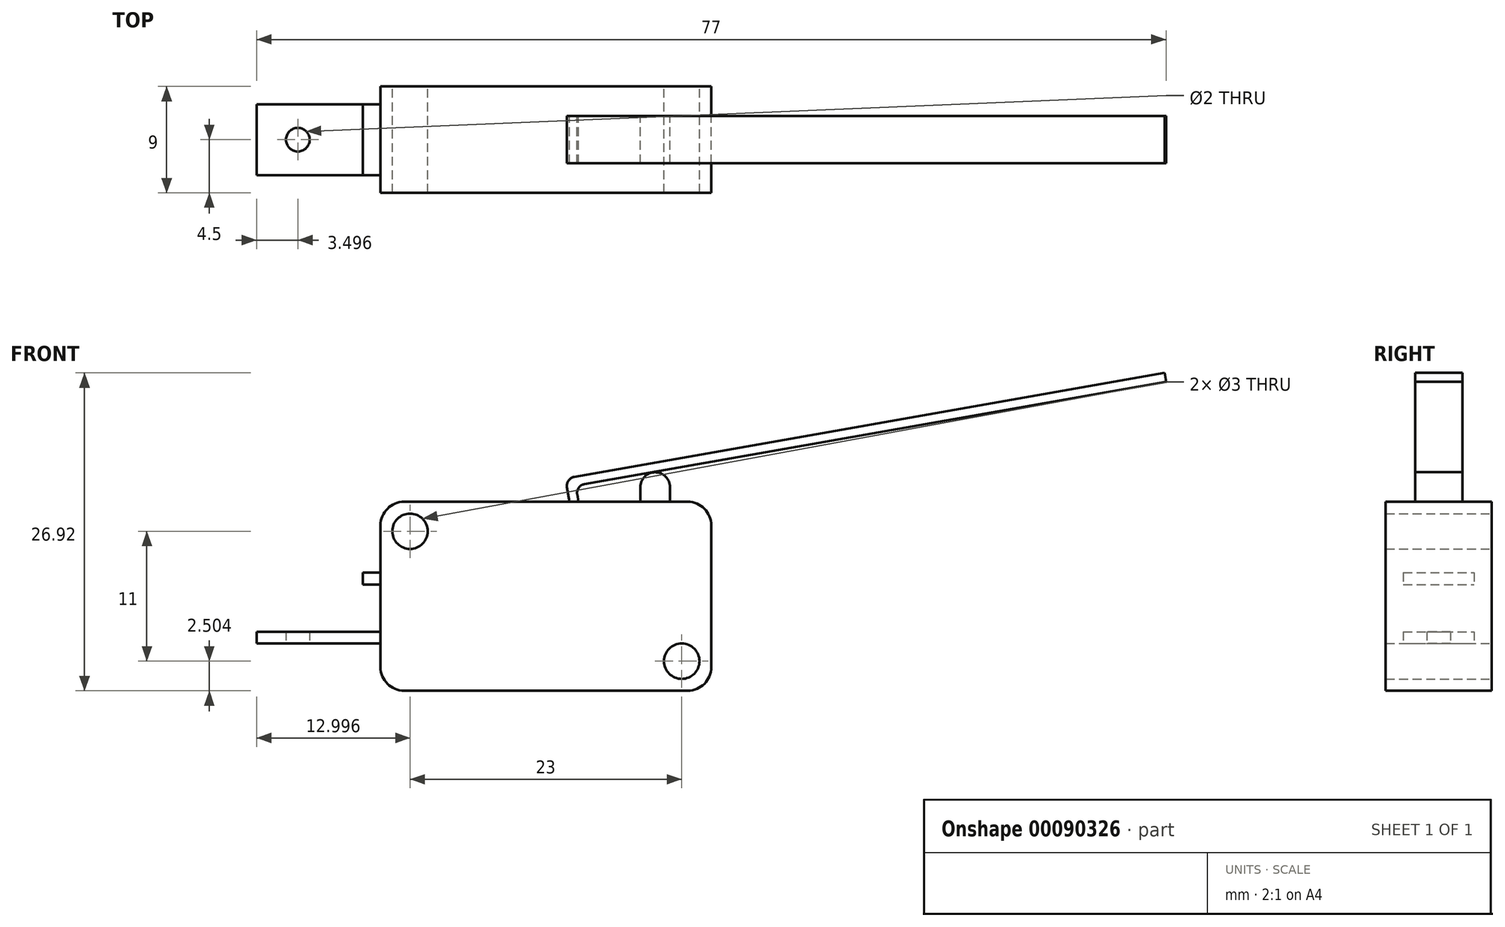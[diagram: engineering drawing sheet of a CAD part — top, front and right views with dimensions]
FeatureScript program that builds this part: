
annotation { "Feature Type Name" : "Feature", "Feature Type Description" : "" }
export const myFeature = defineFeature(function(context is Context, id is Id, definition is map)
    precondition{}
    {
        {
            var Q0;
            Q0=qCreatedBy(makeId("Front.planeOp"),FACE);
            var sketch = newSketch(context, id + "F0", { "sketchPlane" : qUnion([Q0])});
            skLineSegment(sketch, "E0.bottom", {"start": v(2.12, 15.36) * mm, "end": v(26.12, 15.36) * mm});
            skLineSegment(sketch, "E0.top", {"start": v(2.12, -0.64) * mm, "end": v(26.12, -0.64) * mm});
            skLineSegment(sketch, "E0.left", {"start": v(0.12, 13.36) * mm, "end": v(0.12, 1.36) * mm});
            skLineSegment(sketch, "E0.right", {"start": v(28.12, 13.36) * mm, "end": v(28.12, 1.36) * mm});
            skPoint(sketch, "E1.visualSharp", {"position": v(0.12, 15.36) * mm});
            skArc(sketch, "E1.filletArc", {"start": v(2.12, 15.36) * mm, "mid": v(0.7, 14.78) * mm, "end": v(0.12, 13.36) * mm});
            skPoint(sketch, "E2.visualSharp", {"position": v(28.12, 15.36) * mm});
            skArc(sketch, "E2.filletArc", {"start": v(28.12, 13.36) * mm, "mid": v(27.53, 14.78) * mm, "end": v(26.12, 15.36) * mm});
            skPoint(sketch, "E3.visualSharp", {"position": v(28.12, -0.64) * mm});
            skArc(sketch, "E3.filletArc", {"start": v(26.12, -0.64) * mm, "mid": v(27.53, -0.05) * mm, "end": v(28.12, 1.36) * mm});
            skPoint(sketch, "E4.visualSharp", {"position": v(0.12, -0.64) * mm});
            skArc(sketch, "E4.filletArc", {"start": v(0.12, 1.36) * mm, "mid": v(0.7, -0.05) * mm, "end": v(2.12, -0.64) * mm});
            skPoint(sketch, "E5", {"position": v(2.62, 15.36) * mm});
            skPoint(sketch, "E6", {"position": v(0.12, 12.86) * mm});
            skPoint(sketch, "E7", {"position": v(2.62, 12.86) * mm});
            skCircle(sketch, "E8", {"center": v(2.62, 12.86) * mm, "radius": 1.5 * mm});
            skPoint(sketch, "E9", {"position": v(25.62, -0.64) * mm});
            skPoint(sketch, "E10", {"position": v(25.62, 1.86) * mm});
            skCircle(sketch, "E11", {"center": v(25.62, 1.86) * mm, "radius": 1.5 * mm});
            skPoint(sketch, "E12", {"position": v(16.12, 15.36) * mm});
            skPoint(sketch, "E13", {"position": v(0.12, 9.36) * mm});
            skLineSegment(sketch, "E14.bottom", {"start": v(0.12, 9.36) * mm, "end": v(-1.38, 9.36) * mm});
            skLineSegment(sketch, "E14.top", {"start": v(0.12, 8.36) * mm, "end": v(-1.38, 8.36) * mm});
            skLineSegment(sketch, "E14.left", {"start": v(0.12, 9.36) * mm, "end": v(0.12, 8.36) * mm});
            skLineSegment(sketch, "E14.right", {"start": v(-1.38, 9.36) * mm, "end": v(-1.38, 8.36) * mm});
            skLineSegment(sketch, "E15", {"start": v(16.12, 15.36) * mm, "end": v(15.9, 16.6) * mm});
            skLineSegment(sketch, "E16", {"start": v(16.88, 15.36) * mm, "end": v(16.77, 15.99) * mm});
            skLineSegment(sketch, "E17", {"start": v(16.5, 17.46) * mm, "end": v(16.5, 17.46) * mm});
            skLineSegment(sketch, "E18", {"start": v(15.77, 17.33) * mm, "end": v(66.49, 26.28) * mm});
            skLineSegment(sketch, "E19", {"start": v(66.49, 26.28) * mm, "end": v(66.62, 25.54) * mm});
            skLineSegment(sketch, "E20", {"start": v(66.62, 25.54) * mm, "end": v(17.38, 16.86) * mm});
            skPoint(sketch, "E21.visualSharp", {"position": v(15.77, 17.33) * mm});
            skArc(sketch, "E21.filletArc", {"start": v(16.5, 17.46) * mm, "mid": v(16.02, 17.16) * mm, "end": v(15.9, 16.6) * mm});
            skPoint(sketch, "E22.newPointB", {"position": v(16.5, 17.46) * mm});
            skArc(sketch, "E22.filletArc", {"start": v(17.38, 16.86) * mm, "mid": v(16.9, 16.55) * mm, "end": v(16.77, 15.99) * mm});
            skPoint(sketch, "E23", {"position": v(24.62, 15.36) * mm});
            skLineSegment(sketch, "E24.bottom", {"start": v(24.62, 15.36) * mm, "end": v(22.12, 15.36) * mm});
            skLineSegment(sketch, "E24.top", {"start": v(24.62, 16.61) * mm, "end": v(22.12, 16.61) * mm});
            skLineSegment(sketch, "E24.left", {"start": v(24.62, 15.36) * mm, "end": v(24.62, 16.61) * mm});
            skLineSegment(sketch, "E24.right", {"start": v(22.12, 15.36) * mm, "end": v(22.12, 16.61) * mm});
            skCircle(sketch, "E25", {"center": v(23.37, 16.61) * mm, "radius": 1.25 * mm});
            skPoint(sketch, "E26", {"position": v(0.12, 3.36) * mm});
            skLineSegment(sketch, "E27.bottom", {"start": v(0.12, 3.36) * mm, "end": v(-10.38, 3.36) * mm});
            skLineSegment(sketch, "E27.top", {"start": v(0.12, 4.36) * mm, "end": v(-10.38, 4.36) * mm});
            skLineSegment(sketch, "E27.left", {"start": v(0.12, 3.36) * mm, "end": v(0.12, 4.36) * mm});
            skLineSegment(sketch, "E27.right", {"start": v(-10.38, 3.36) * mm, "end": v(-10.38, 4.36) * mm});
            skPoint(sketch, "E28", {"position": v(11.62, -0.64) * mm});
            skLineSegment(sketch, "E29.bottom", {"start": v(11.62, -0.64) * mm, "end": v(12.37, -0.64) * mm});
            skLineSegment(sketch, "E29.left", {"start": v(11.62, -0.64) * mm, "end": v(11.62, -3.87) * mm});
            skLineSegment(sketch, "E29.right", {"start": v(12.37, -0.64) * mm, "end": v(12.37, -3.37) * mm});
            skLineSegment(sketch, "E30.bottom", {"start": v(10.87, -4.87) * mm, "end": v(2.87, -4.87) * mm});
            skLineSegment(sketch, "E30.top", {"start": v(11.12, -4.37) * mm, "end": v(2.87, -4.37) * mm});
            skLineSegment(sketch, "E30.right", {"start": v(2.87, -4.87) * mm, "end": v(2.87, -4.37) * mm});
            skPoint(sketch, "E31.visualSharp", {"position": v(12.37, -4.87) * mm});
            skArc(sketch, "E31.filletArc", {"start": v(10.87, -4.87) * mm, "mid": v(11.93, -4.43) * mm, "end": v(12.37, -3.37) * mm});
            skPoint(sketch, "E32.newPointB", {"position": v(13.76, -4.37) * mm});
            skArc(sketch, "E32.filletArc", {"start": v(11.12, -4.37) * mm, "mid": v(11.47, -4.22) * mm, "end": v(11.62, -3.87) * mm});
            skLineSegment(sketch, "E33", {"start": v(66.49, 26.28) * mm, "end": v(-10.38, 26.28) * mm});
            skLineSegment(sketch, "E34", {"start": v(-10.38, 26.28) * mm, "end": v(-10.38, 4.36) * mm});
            skSolve(sketch);
        }
        {
            var Q0;
            Q0=makeQuery(id+"F0.imprint","IMPRINT",FACE,{"disambiguationData":[TD([[makeQuery(id+"F0.imprint","IMPRINT",EDGE,{"derivedFrom":sQuery(id+"F0.wireOp",EDGE,"E0.right")}),-1.0]])]});
            extrude(context, id + "F1", {"entities" : qUnion([Q0]), "depth" : 4.5 * mm});
        }
        {
            var Q0;
            Q0=makeQuery(id+"F0.imprint","IMPRINT",FACE,{"disambiguationData":[TD([[makeQuery(id+"F0.imprint","IMPRINT",EDGE,{"derivedFrom":sQuery(id+"F0.wireOp",EDGE,"E14.bottom")}),1.0]])]});
            var Q1;
            Q1=makeQuery(id+"F0.imprint","IMPRINT",FACE,{"disambiguationData":[TD([[makeQuery(id+"F0.imprint","IMPRINT",EDGE,{"derivedFrom":sQuery(id+"F0.wireOp",EDGE,"E27.bottom")}),-1.0]])]});
            var Q2;
            Q2=makeQuery(id+"F0.imprint","IMPRINT",FACE,{"disambiguationData":[TD([[makeQuery(id+"F0.imprint","IMPRINT",EDGE,{"derivedFrom":sQuery(id+"F0.wireOp",EDGE,"E29.bottom")}),-1.0]])]});
            extrude(context, id + "F2", {"entities" : qUnion([Q0, Q1, Q2]), "operationType" : NewBodyOperationType.ADD, "depth" : 3 * mm});
        }
        {
            var Q0;
            {var subQ4=sQuery(id+"F0.wireOp",EDGE,"E15");Q0=makeQuery(id+"F0.imprint","IMPRINT",FACE,{"disambiguationData":[TD([[makeQuery(id+"F0.imprint","IMPRINT",EDGE,{"derivedFrom":subQ4}),-1.0]])]});}
            var Q1;
            {var subQ0=sQuery(id+"F0.wireOp",EDGE,"E24.left");Q1=makeQuery(id+"F0.imprint","IMPRINT",FACE,{"disambiguationData":[TD([[makeQuery(id+"F0.imprint","IMPRINT",EDGE,{"derivedFrom":subQ0}),1.0]])]});}
            var Q2;
            {var subQ0=sQuery(id+"F0.wireOp",EDGE,"E24.right");Q2=makeQuery(id+"F0.imprint","IMPRINT",FACE,{"disambiguationData":[TD([[makeQuery(id+"F0.imprint","IMPRINT",EDGE,{"derivedFrom":subQ0}),-1.0]])]});}
            var Q3;
            {var subQ0=sQuery(id+"F0.wireOp",EDGE,"E24.top");Q3=makeQuery(id+"F0.imprint","IMPRINT",FACE,{"disambiguationData":[TD([[makeQuery(id+"F0.imprint","IMPRINT",EDGE,{"derivedFrom":subQ0}),1.0]])]});}
            var Q4;
            {var subQ0=sQuery(id+"F0.wireOp",EDGE,"E24.top");Q4=makeQuery(id+"F0.imprint","IMPRINT",FACE,{"disambiguationData":[TD([[makeQuery(id+"F0.imprint","IMPRINT",EDGE,{"derivedFrom":subQ0}),-1.0]])]});}
            extrude(context, id + "F3", {"entities" : qUnion([Q0, Q1, Q2, Q3, Q4]), "operationType" : NewBodyOperationType.ADD, "depth" : 2 * mm});
        }
        {
            var Q0;
            Q0=makeQuery(id+"F0.imprint","IMPRINT",FACE,{"disambiguationData":[TD([[makeQuery(id+"F0.imprint","IMPRINT",EDGE,{"derivedFrom":sQuery(id+"F0.wireOp",EDGE,"E0.right")}),-1.0]])]});
            extrude(context, id + "F4", {"entities" : qUnion([Q0]), "operationType" : NewBodyOperationType.ADD, "oppositeDirection" : true, "depth" : 4.5 * mm});
        }
        {
            var Q0;
            Q0=makeQuery(id+"F0.imprint","IMPRINT",FACE,{"disambiguationData":[TD([[makeQuery(id+"F0.imprint","IMPRINT",EDGE,{"derivedFrom":sQuery(id+"F0.wireOp",EDGE,"E14.bottom")}),1.0]])]});
            var Q1;
            Q1=makeQuery(id+"F0.imprint","IMPRINT",FACE,{"disambiguationData":[TD([[makeQuery(id+"F0.imprint","IMPRINT",EDGE,{"derivedFrom":sQuery(id+"F0.wireOp",EDGE,"E27.bottom")}),-1.0]])]});
            var Q2;
            Q2=makeQuery(id+"F0.imprint","IMPRINT",FACE,{"disambiguationData":[TD([[makeQuery(id+"F0.imprint","IMPRINT",EDGE,{"derivedFrom":sQuery(id+"F0.wireOp",EDGE,"E29.bottom")}),-1.0]])]});
            extrude(context, id + "F5", {"entities" : qUnion([Q0, Q1, Q2]), "operationType" : NewBodyOperationType.ADD, "oppositeDirection" : true, "depth" : 3 * mm});
        }
        {
            var Q0;
            {var subQ0=sQuery(id+"F0.wireOp",EDGE,"E24.top");Q0=makeQuery(id+"F0.imprint","IMPRINT",FACE,{"disambiguationData":[TD([[makeQuery(id+"F0.imprint","IMPRINT",EDGE,{"derivedFrom":subQ0}),-1.0]])]});}
            var Q1;
            {var subQ0=sQuery(id+"F0.wireOp",EDGE,"E24.top");Q1=makeQuery(id+"F0.imprint","IMPRINT",FACE,{"disambiguationData":[TD([[makeQuery(id+"F0.imprint","IMPRINT",EDGE,{"derivedFrom":subQ0}),1.0]])]});}
            var Q2;
            {var subQ0=sQuery(id+"F0.wireOp",EDGE,"E24.left");Q2=makeQuery(id+"F0.imprint","IMPRINT",FACE,{"disambiguationData":[TD([[makeQuery(id+"F0.imprint","IMPRINT",EDGE,{"derivedFrom":subQ0}),1.0]])]});}
            var Q3;
            {var subQ0=sQuery(id+"F0.wireOp",EDGE,"E24.right");Q3=makeQuery(id+"F0.imprint","IMPRINT",FACE,{"disambiguationData":[TD([[makeQuery(id+"F0.imprint","IMPRINT",EDGE,{"derivedFrom":subQ0}),-1.0]])]});}
            var Q4;
            {var subQ4=sQuery(id+"F0.wireOp",EDGE,"E15");Q4=makeQuery(id+"F0.imprint","IMPRINT",FACE,{"disambiguationData":[TD([[makeQuery(id+"F0.imprint","IMPRINT",EDGE,{"derivedFrom":subQ4}),-1.0]])]});}
            extrude(context, id + "F6", {"entities" : qUnion([Q0, Q1, Q2, Q3, Q4]), "operationType" : NewBodyOperationType.ADD, "oppositeDirection" : true, "depth" : 2 * mm});
        }
        {
            var Q0;
            {var subQ0=sQuery(id+"F0.wireOp",EDGE,"E30.bottom");Q0=makeQuery(id+"F5.boolean.opBoolean","MERGE",FACE,{"derivedFrom":[makeQuery(id+"F2.opExtrude","SWEPT_FACE",FACE,{"disambiguationData":[OSD([subQ0])]}),makeQuery(id+"F5.opExtrude","SWEPT_FACE",FACE,{"disambiguationData":[OSD([subQ0])]})]});}
            var sketch = newSketch(context, id + "F7", { "sketchPlane" : qUnion([Q0])});
            skPoint(sketch, "E35", {"position": v(2.87, 0) * mm});
            skLineSegment(sketch, "E36", {"start": v(2.87, 0) * mm, "end": v(5.37, 0) * mm});
            skSolve(sketch);
        }
        {
            var Q0;
            {var subQ0=sQuery(id+"F0.wireOp",EDGE,"E27.bottom");Q0=makeQuery(id+"F5.boolean.opBoolean","MERGE",FACE,{"derivedFrom":[makeQuery(id+"F2.opExtrude","SWEPT_FACE",FACE,{"disambiguationData":[OSD([subQ0])]}),makeQuery(id+"F5.opExtrude","SWEPT_FACE",FACE,{"disambiguationData":[OSD([subQ0])]})]});}
            var sketch = newSketch(context, id + "F8", { "sketchPlane" : qUnion([Q0])});
            skPoint(sketch, "E37", {"position": v(-10.38, 0) * mm});
            skLineSegment(sketch, "E38", {"start": v(-10.38, 0) * mm, "end": v(-6.88, 0) * mm});
            skSolve(sketch);
        }
        {
            var Q0;
            Q0=sQuery(id+"F7.wireOp",VERTEX,"E36.end");
            var Q1;
            Q1=sQuery(id+"F8.wireOp",VERTEX,"E38.end");
            var Q2;
            Q2=makeQuery(id+"F1.opExtrude","SWEPT_BODY",BODY,{"disambiguationData":[OSD([sQuery(id+"F0.wireOp",EDGE,"E0.bottom"),sQuery(id+"F0.wireOp",EDGE,"E0.top"),sQuery(id+"F0.wireOp",EDGE,"E0.left"),sQuery(id+"F0.wireOp",EDGE,"E0.right"),sQuery(id+"F0.wireOp",EDGE,"E1.filletArc"),sQuery(id+"F0.wireOp",EDGE,"E2.filletArc"),sQuery(id+"F0.wireOp",EDGE,"E3.filletArc"),sQuery(id+"F0.wireOp",EDGE,"E4.filletArc"),sQuery(id+"F0.wireOp",EDGE,"E8"),sQuery(id+"F0.wireOp",EDGE,"E11"),sQuery(id+"F0.wireOp",EDGE,"E14.left"),sQuery(id+"F0.wireOp",EDGE,"E24.bottom"),sQuery(id+"F0.wireOp",EDGE,"E27.left"),sQuery(id+"F0.wireOp",EDGE,"E29.bottom")])]});
            hole(context, id + "F9", {"style" : HoleStyle.SIMPLE, "endStyle" : HoleEndStyle.BLIND, "holeDiameter" : 2 * mm, "holeDepth" : 1 * mm, "locations" : qUnion([Q0, Q1]), "scope" : qUnion([Q2])});
        }
    });
